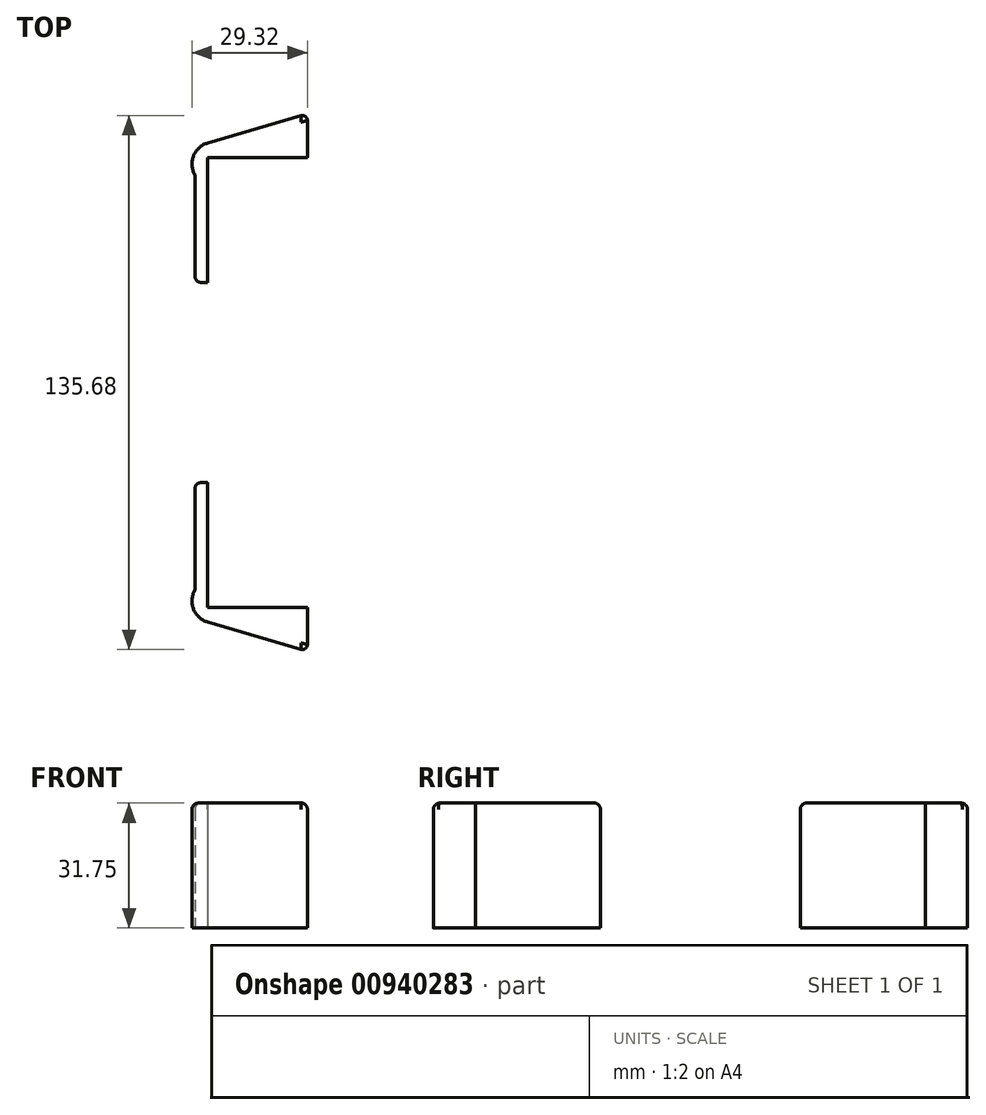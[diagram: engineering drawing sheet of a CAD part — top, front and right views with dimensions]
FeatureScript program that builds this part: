
annotation { "Feature Type Name" : "Feature", "Feature Type Description" : "" }
export const myFeature = defineFeature(function(context is Context, id is Id, definition is map)
    precondition{}
    {
        {
            var Q0;
            Q0=qCreatedBy(makeId("Top.planeOp"),FACE);
            var sketch = newSketch(context, id + "F0", { "sketchPlane" : qUnion([Q0])});
            skLineSegment(sketch, "E0", {"start": v(0, 0) * mm, "end": v(0, 31.75) * mm});
            skLineSegment(sketch, "E1", {"start": v(0, 31.75) * mm, "end": v(25.4, 31.75) * mm});
            skLineSegment(sketch, "E2", {"start": v(25.4, 31.75) * mm, "end": v(25.4, 42.86) * mm});
            skLineSegment(sketch, "E3", {"start": v(25.4, 42.86) * mm, "end": v(0.04, 35.45) * mm});
            skLineSegment(sketch, "E4", {"start": v(0, 0) * mm, "end": v(-3.17, 0) * mm});
            skArc(sketch, "E5", {"start": v(0.04, 35.45) * mm, "mid": v(-3.46, 32.37) * mm, "end": v(-3.34, 27.7) * mm});
            skLineSegment(sketch, "E6", {"start": v(-3.17, 0) * mm, "end": v(-3.17, 26.99) * mm});
            skArc(sketch, "E7", {"start": v(-3.18, 26.99) * mm, "mid": v(-3.22, 27.35) * mm, "end": v(-3.34, 27.7) * mm});
            skSolve(sketch);
        }
        {
            var Q0;
            Q0=makeQuery(id+"F0.imprint","IMPRINT",FACE,{"disambiguationData":[TD([[makeQuery(id+"F0.imprint","IMPRINT",EDGE,{"derivedFrom":sQuery(id+"F0.wireOp",EDGE,"E0")}),1.0]])]});
            extrude(context, id + "F1", {"entities" : qUnion([Q0]), "depth" : 31.75 * mm, "offsetDistance" : 25.4 * mm});
        }
        {
            var Q0;
            Q0=makeQuery(id+"F1.opExtrude","CAP_EDGE",EDGE,{"disambiguationData":[OSD([sQuery(id+"F0.wireOp",EDGE,"E4")])],"isStart":false});
            var Q1;
            Q1=makeQuery(id+"F1.opExtrude","CAP_EDGE",EDGE,{"disambiguationData":[OSD([sQuery(id+"F0.wireOp",EDGE,"QeGOZpxM-Z9X6-TqyO-8uy4-hr4jBhoiYynM")])],"isStart":false});
            var Q2;
            Q2=makeQuery(id+"F1.opExtrude","CAP_EDGE",EDGE,{"disambiguationData":[OSD([sQuery(id+"F0.wireOp",EDGE,"E2")])],"isStart":false});
            var Q3;
            Q3=makeQuery(id+"F1.opExtrude","CAP_EDGE",EDGE,{"disambiguationData":[OSD([sQuery(id+"F0.wireOp",EDGE,"E6")])],"isStart":false});
            var Q4;
            Q4=makeQuery(id+"F1.opExtrude","SWEPT_EDGE",EDGE,{"disambiguationData":[OSD([sQuery(id+"F0.wireOp",EDGE,"E4"),sQuery(id+"F0.wireOp",EDGE,"E6")])]});
            fillet(context, id + "F2", {"entities" : qUnion([Q0, Q1, Q2, Q3, Q4]), "radius" : 1.59 * mm, "tangentPropagation" : true, "allowEdgeOverflow" : false});
        }
        {
            var Q0;
            Q0=qCreatedBy(makeId("Front.planeOp"),FACE);
            cPlane(context, id + "F3", {"entities" : qUnion([Q0]), "cplaneType" : CPlaneType.OFFSET, "offset" : 25.4 * mm, "width" : 152.4 * mm, "height" : 152.4 * mm});
        }
        {
            var Q0;
            Q0=makeQuery(id+"F1.opExtrude","SWEPT_EDGE",EDGE,{"disambiguationData":[OSD([sQuery(id+"F0.wireOp",EDGE,"E2"),sQuery(id+"F0.wireOp",EDGE,"E3")])]});
            fillet(context, id + "F4", {"entities" : qUnion([Q0]), "radius" : 1.27 * mm, "tangentPropagation" : true, "allowEdgeOverflow" : false});
        }
        {
            var Q0;
            Q0=makeQuery(id+"F1.opExtrude","SWEPT_BODY",BODY,{"disambiguationData":[OSD([sQuery(id+"F0.wireOp",EDGE,"E0"),sQuery(id+"F0.wireOp",EDGE,"E1"),sQuery(id+"F0.wireOp",EDGE,"E2"),sQuery(id+"F0.wireOp",EDGE,"E3"),sQuery(id+"F0.wireOp",EDGE,"E4"),sQuery(id+"F0.wireOp",EDGE,"QeGOZpxM-Z9X6-TqyO-8uy4-hr4jBhoiYynM"),sQuery(id+"F0.wireOp",EDGE,"E5")])]});
            var Q1;
            Q1=qCreatedBy(id+"F3.planeOp",FACE);
            mirror(context, id + "F5", {"entities" : qUnion([Q0]), "mirrorPlane" : qUnion([Q1])});
        }
    });
